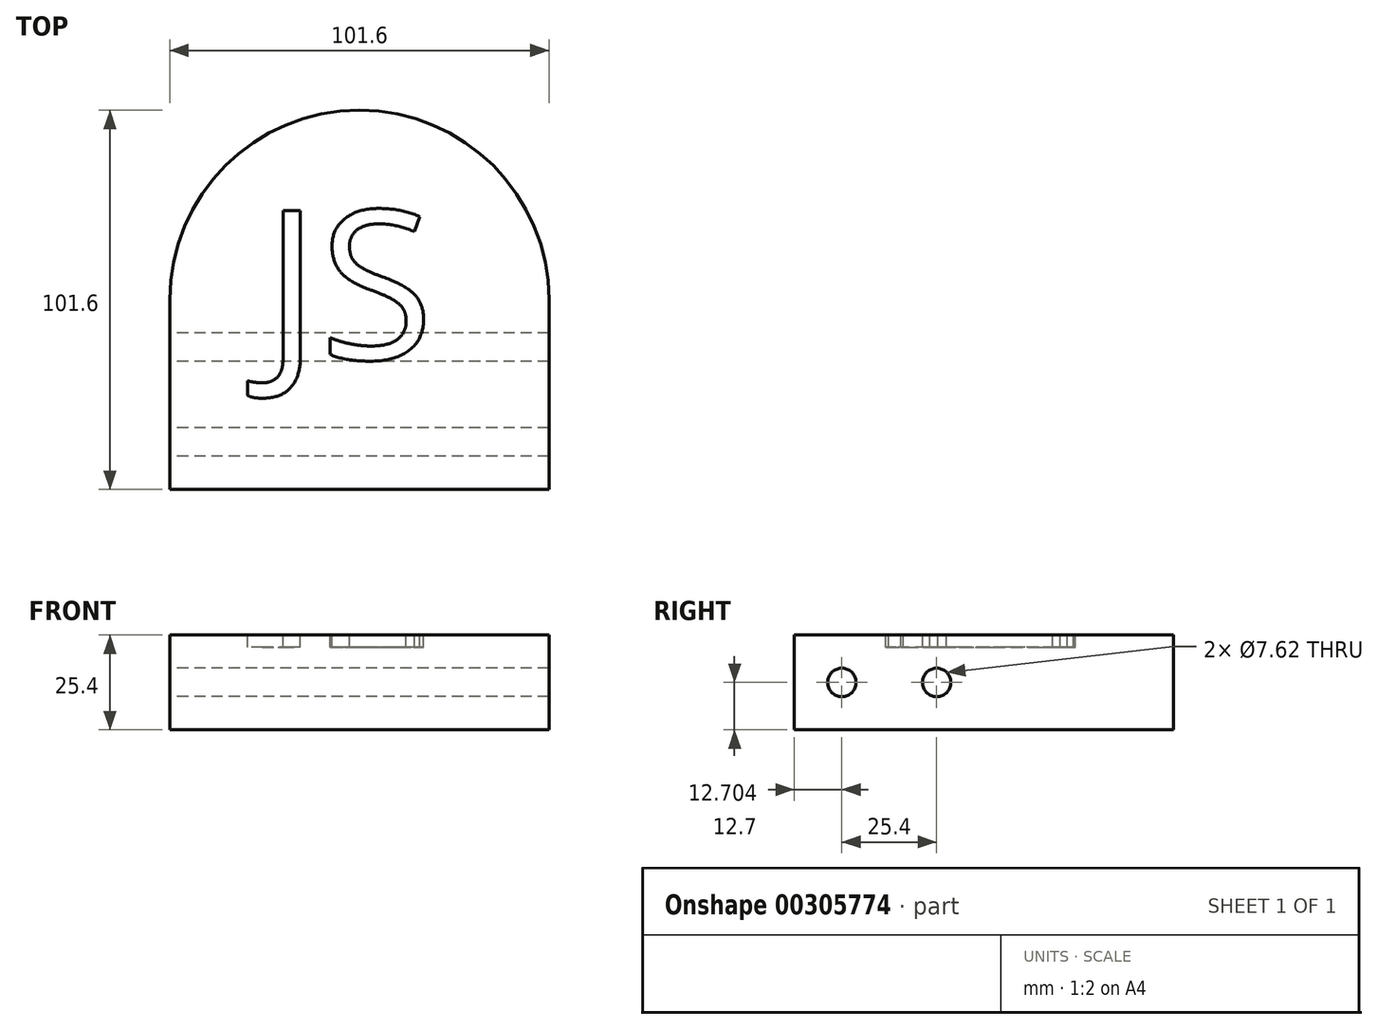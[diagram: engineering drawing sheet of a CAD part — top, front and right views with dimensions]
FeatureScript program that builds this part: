
annotation { "Feature Type Name" : "Feature", "Feature Type Description" : "" }
export const myFeature = defineFeature(function(context is Context, id is Id, definition is map)
    precondition{}
    {
        {
            var Q0;
            Q0=qCreatedBy(makeId("Top.planeOp"),FACE);
            var sketch = newSketch(context, id + "F0", { "sketchPlane" : qUnion([Q0])});
            skLineSegment(sketch, "E0.bottom", {"start": v(-46.19, 27.55) * mm, "end": v(55.41, 27.55) * mm});
            skLineSegment(sketch, "E0.top", {"start": v(-46.19, -23.25) * mm, "end": v(55.41, -23.25) * mm});
            skLineSegment(sketch, "E0.left", {"start": v(-46.19, 27.55) * mm, "end": v(-46.19, -23.25) * mm});
            skLineSegment(sketch, "E0.right", {"start": v(55.41, 27.55) * mm, "end": v(55.41, -23.25) * mm});
            skArc(sketch, "E1", {"start": v(55.41, 27.55) * mm, "mid": v(4.61, 78.35) * mm, "end": v(-46.19, 27.55) * mm});
            skSolve(sketch);
        }
        {
            var Q0;
            Q0=makeQuery(id+"F0.imprint","IMPRINT",FACE,{"disambiguationData":[TD([[makeQuery(id+"F0.imprint","IMPRINT",EDGE,{"derivedFrom":sQuery(id+"F0.wireOp",EDGE,"E0.bottom")}),1.0]])]});
            var Q1;
            Q1=makeQuery(id+"F0.imprint","IMPRINT",FACE,{"disambiguationData":[TD([[makeQuery(id+"F0.imprint","IMPRINT",EDGE,{"derivedFrom":sQuery(id+"F0.wireOp",EDGE,"E0.bottom")}),-1.0]])]});
            extrude(context, id + "F1", {"entities" : qUnion([Q0, Q1]), "oppositeDirection" : true, "depth" : 25.4 * mm});
        }
        {
            var Q0;
            Q0=makeQuery(id+"F1.opExtrude","SWEPT_FACE",FACE,{"disambiguationData":[OSD([sQuery(id+"F0.wireOp",EDGE,"E0.left")])]});
            var sketch = newSketch(context, id + "F2", { "sketchPlane" : qUnion([Q0])});
            skLineSegment(sketch, "E2", {"start": v(-27.55, -12.7) * mm, "end": v(23.25, -12.7) * mm, "construction": true});
            skCircle(sketch, "E3", {"center": v(10.55, -12.7) * mm, "radius": 3.81 * mm});
            skCircle(sketch, "E4", {"center": v(-14.85, -12.7) * mm, "radius": 3.81 * mm});
            skSolve(sketch);
        }
        {
            var Q0;
            Q0=makeQuery(id+"F2.imprint","IMPRINT",FACE,{"disambiguationData":[TD([[makeQuery(id+"F2.imprint","IMPRINT",EDGE,{"derivedFrom":sQuery(id+"F2.wireOp",EDGE,"E4")}),1.0]])]});
            var Q1;
            Q1=makeQuery(id+"F2.imprint","IMPRINT",FACE,{"disambiguationData":[TD([[makeQuery(id+"F2.imprint","IMPRINT",EDGE,{"derivedFrom":sQuery(id+"F2.wireOp",EDGE,"E3")}),1.0]])]});
            extrude(context, id + "F3", {"entities" : qUnion([Q0, Q1]), "operationType" : NewBodyOperationType.REMOVE, "oppositeDirection" : true, "depth" : 101.6 * mm});
        }
        {
            var Q0;
            Q0=makeQuery(id+"F1.opExtrude","CAP_FACE",FACE,{"disambiguationData":[OSD([sQuery(id+"F0.wireOp",EDGE,"E0.top"),sQuery(id+"F0.wireOp",EDGE,"E0.left"),sQuery(id+"F0.wireOp",EDGE,"E0.right"),sQuery(id+"F0.wireOp",EDGE,"E1")])],"isStart":true});
            var sketch = newSketch(context, id + "F4", { "sketchPlane" : qUnion([Q0])});
            skText(sketch, "E5", { "text": "JS", "fontName": "OpenSans-Regular.ttf"});
            const initialGuessF4  = {"E5": [-0.021, 0.01167, 1, 0, 0.04015]};
            skSetInitialGuess(sketch, initialGuessF4);
            skSolve(sketch);
        }
        {
            var Q0;
            Q0 = qSketchRegion(id + "F4", true);
            extrude(context, id + "F5", {"entities" : qUnion([Q0]), "operationType" : NewBodyOperationType.REMOVE, "oppositeDirection" : true, "depth" : 3.3 * mm});
        }
    });
